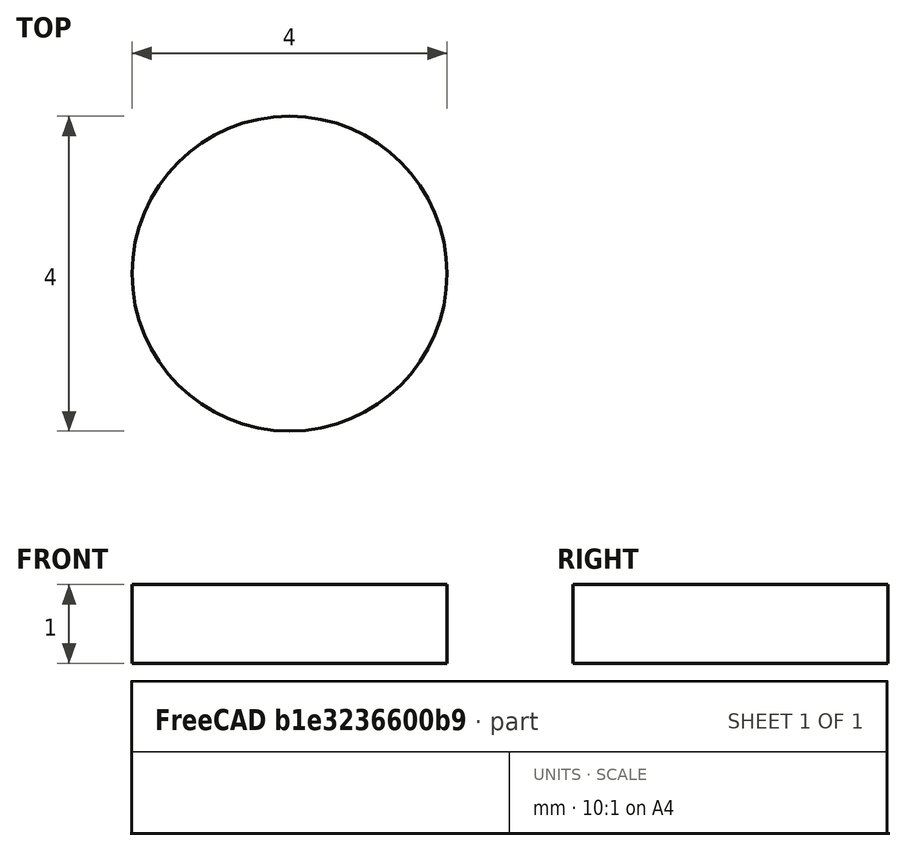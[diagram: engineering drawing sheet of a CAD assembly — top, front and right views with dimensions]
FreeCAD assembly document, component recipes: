
FREECAD ASSEMBLY — COMPONENT RECIPES ("external-file")

This assembly document has 2 components, labeled P0..P1 below (a component is one placed body or linked part). 0 of them carry a construction recipe — the FreeCAD feature program that regenerates the part from scratch, quoted from this document or its linked companion documents; the rest are supplied as boundary geometry only. No exploded tour is included for this assembly.
COMPONENT P0 — geometry summary ("Part"; no construction recipe available for this part):
  bounding box: 4.0 x 4.0 x 1.0 mm
  tessellated surface: 500 triangles
  volume: 13 mm^3 (79% of its bounding box)
  symmetry: 2-fold rotationally symmetric about the x axis; 2-fold rotationally symmetric about the y axis; revolution-symmetric about the z axis through its bounding-box center; mirror-symmetric across its x mid-plane, y mid-plane, z mid-plane
COMPONENT P1 — geometry summary ("link-lens"; no construction recipe available for this part):
  bounding box: 4.0 x 4.0 x 1.0 mm
  tessellated surface: 2,308 triangles
  volume: 7 mm^3 (46% of its bounding box)
  symmetry: 2-fold rotationally symmetric about the x axis; 2-fold rotationally symmetric about the y axis; revolution-symmetric about the z axis through its bounding-box center; mirror-symmetric across its x mid-plane, y mid-plane, z mid-plane
PROVENANCE & LICENSES
A FreeCAD (.FCStd) document from a public repository crawl; recipes are the document's own serialized feature recipes (and, for linked parts, companion documents' recipes).
License: lgpl-3.0.
